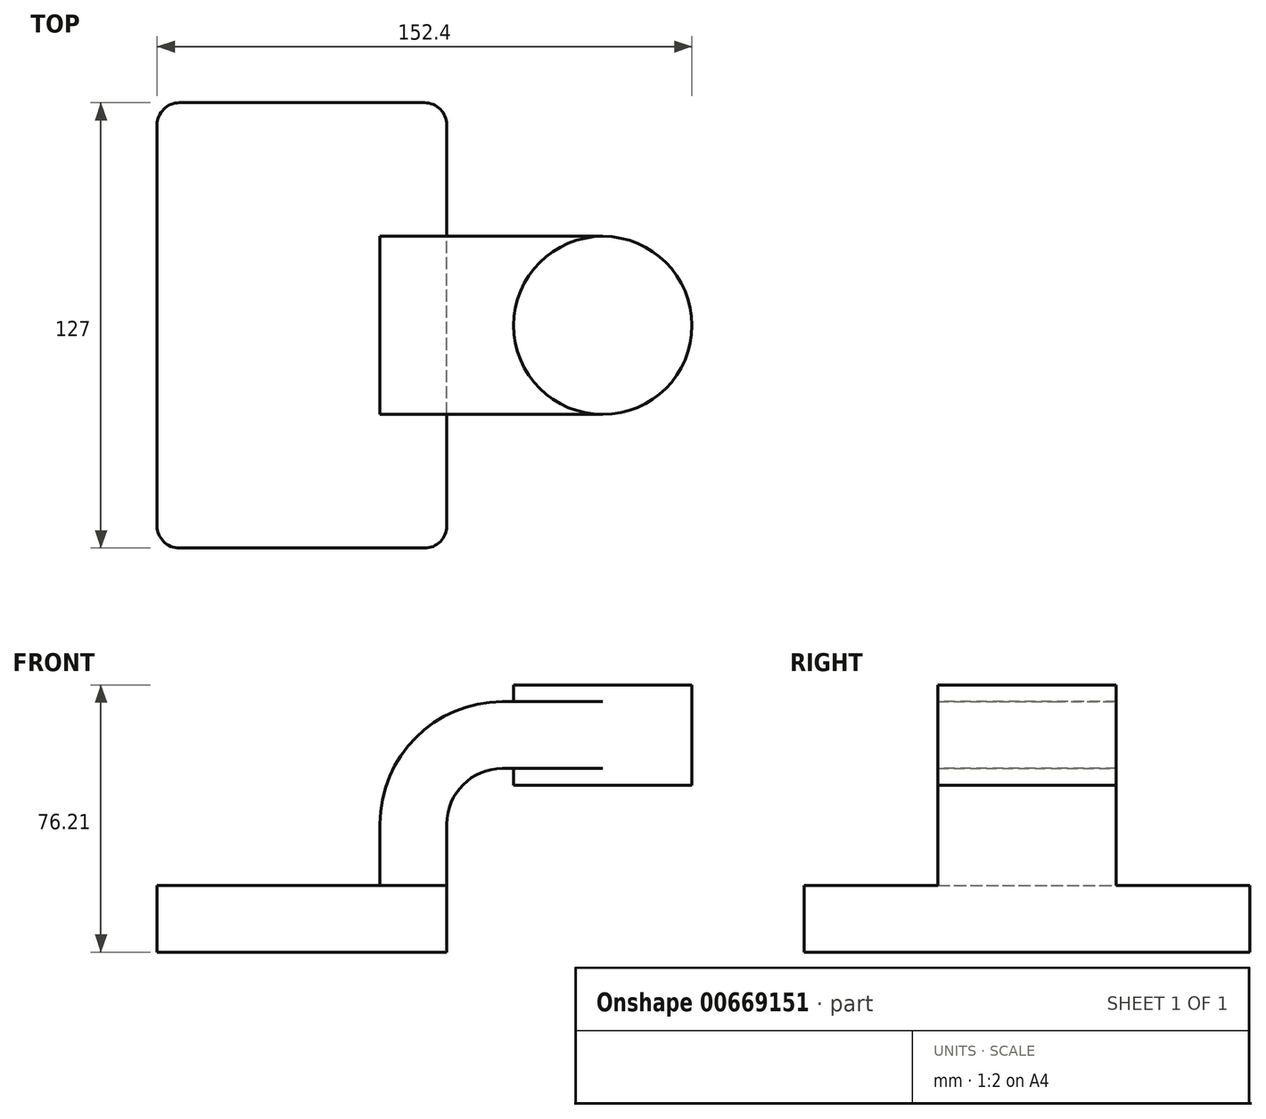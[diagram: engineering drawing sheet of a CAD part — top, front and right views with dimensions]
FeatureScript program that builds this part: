
annotation { "Feature Type Name" : "Feature", "Feature Type Description" : "" }
export const myFeature = defineFeature(function(context is Context, id is Id, definition is map)
    precondition{}
    {
        {
            var Q0;
            Q0=qCreatedBy(makeId("Front.planeOp"),FACE);
            var sketch = newSketch(context, id + "F0", { "sketchPlane" : qUnion([Q0])});
            skLineSegment(sketch, "E0.bottom", {"start": v(-41.28, 9.52) * mm, "end": v(41.28, 9.53) * mm});
            skLineSegment(sketch, "E0.top", {"start": v(-41.28, -9.53) * mm, "end": v(41.28, -9.53) * mm});
            skLineSegment(sketch, "E0.left", {"start": v(-41.28, 9.52) * mm, "end": v(-41.28, -9.53) * mm});
            skLineSegment(sketch, "E0.right", {"start": v(41.28, 9.53) * mm, "end": v(41.28, -9.52) * mm});
            skPoint(sketch, "E0.middle", {"position": v(0, 0) * mm});
            skLineSegment(sketch, "E1.bottom", {"start": v(60.32, 66.67) * mm, "end": v(111.12, 66.67) * mm});
            skLineSegment(sketch, "E1.top", {"start": v(60.32, 38.1) * mm, "end": v(111.12, 38.1) * mm});
            skLineSegment(sketch, "E1.left", {"start": v(60.32, 66.67) * mm, "end": v(60.32, 38.1) * mm});
            skLineSegment(sketch, "E1.right", {"start": v(111.12, 66.67) * mm, "end": v(111.12, 38.1) * mm});
            skPoint(sketch, "E1.middle", {"position": v(85.72, 52.39) * mm});
            skLineSegment(sketch, "E2", {"start": v(41.27, 9.53) * mm, "end": v(41.27, 26.99) * mm});
            skArc(sketch, "E3", {"start": v(41.27, 26.99) * mm, "mid": v(45.92, 38.21) * mm, "end": v(57.15, 42.86) * mm});
            skLineSegment(sketch, "E4", {"start": v(57.15, 42.86) * mm, "end": v(85.72, 42.86) * mm});
            skLineSegment(sketch, "E5.0", {"start": v(57.15, 61.91) * mm, "end": v(85.72, 61.91) * mm});
            skArc(sketch, "E5.1", {"start": v(22.23, 26.99) * mm, "mid": v(32.45, 51.68) * mm, "end": v(57.15, 61.91) * mm});
            skLineSegment(sketch, "E5.2", {"start": v(22.22, 9.53) * mm, "end": v(22.22, 26.99) * mm});
            skFitSpline(sketch, "E6", {"points": [v(-41.28, 9.52) * mm, v(57.15, 61.91) * mm], "startDerivative": vector(60.01, 126.68) * mm, "endDerivative": vector(125.56, 0.13) * mm});
            skLineSegment(sketch, "E7", {"start": v(85.72, 66.67) * mm, "end": v(85.72, 38.1) * mm});
            skSolve(sketch);
        }
        {
            var Q0;
            Q0=makeQuery(id+"F0.imprint","IMPRINT",FACE,{"disambiguationData":[TD([[makeQuery(id+"F0.imprint","IMPRINT",EDGE,{"derivedFrom":sQuery(id+"F0.wireOp",EDGE,"E0.top")}),1.0]])]});
            extrude(context, id + "F1", {"entities" : qUnion([Q0]), "endBound" : BoundingType.SYMMETRIC, "depth" : 127 * mm, "offsetDistance" : 25.4 * mm});
        }
        {
            var Q0;
            {var subQ1=sQuery(id+"F0.wireOp",EDGE,"E2");Q0=makeQuery(id+"F0.imprint","IMPRINT",FACE,{"disambiguationData":[TD([[makeQuery(id+"F0.imprint","IMPRINT",EDGE,{"derivedFrom":subQ1}),1.0]])]});}
            var Q1;
            {var subQ0=sQuery(id+"F0.wireOp",EDGE,"E5.0");var subQ1=sQuery(id+"F0.wireOp",EDGE,"E1.left");var subQ2=makeQuery(id+"F0.imprint","INTERSECT",VERTEX,{"derivedFrom":[subQ1,subQ0]});Q1=makeQuery(id+"F0.imprint","IMPRINT",FACE,{"disambiguationData":[TD([[makeQuery(id+"F0.imprint","IMPRINT",EDGE,{"disambiguationData":[TD([[subQ2,-1.0]])],"derivedFrom":subQ1}),1.0]])]});}
            extrude(context, id + "F2", {"entities" : qUnion([Q0, Q1]), "operationType" : NewBodyOperationType.ADD, "endBound" : BoundingType.SYMMETRIC, "depth" : 50.8 * mm, "offsetDistance" : 25.4 * mm});
        }
        {
            var Q0;
            {var subQ4=sQuery(id+"F0.wireOp",EDGE,"E5.1");Q0=makeQuery(id+"F0.imprint","IMPRINT",FACE,{"disambiguationData":[TD([[makeQuery(id+"F0.imprint","IMPRINT",EDGE,{"derivedFrom":subQ4}),1.0]])]});}
            extrude(context, id + "F3", {"entities" : qUnion([Q0]), "operationType" : NewBodyOperationType.ADD, "endBound" : BoundingType.SYMMETRIC, "depth" : 15.88 * mm, "offsetDistance" : 25.4 * mm});
        }
        {
            var Q0;
            {var subQ0=sQuery(id+"F0.wireOp",EDGE,"E1.right");Q0=makeQuery(id+"F0.imprint","IMPRINT",FACE,{"disambiguationData":[TD([[makeQuery(id+"F0.imprint","IMPRINT",EDGE,{"derivedFrom":subQ0}),-1.0]])]});}
            var Q1;
            Q1=sQuery(id+"F0.wireOp",EDGE,"E7");
            revolve(context, id + "F4", {"operationType" : NewBodyOperationType.ADD, "entities" : qUnion([Q0]), "axis" : qUnion([Q1]), "revolveType" : RevolveType.FULL});
        }
        {
            var Q0;
            Q0=makeQuery(id+"F1.opExtrude","CAP_EDGE",EDGE,{"disambiguationData":[OSD([sQuery(id+"F0.wireOp",EDGE,"E0.right")])],"isStart":false});
            var Q1;
            Q1=makeQuery(id+"F1.opExtrude","CAP_EDGE",EDGE,{"disambiguationData":[OSD([sQuery(id+"F0.wireOp",EDGE,"E0.left")])],"isStart":false});
            var Q2;
            Q2=makeQuery(id+"F1.opExtrude","CAP_EDGE",EDGE,{"disambiguationData":[OSD([sQuery(id+"F0.wireOp",EDGE,"E0.right")])],"isStart":true});
            var Q3;
            Q3=makeQuery(id+"F1.opExtrude","CAP_EDGE",EDGE,{"disambiguationData":[OSD([sQuery(id+"F0.wireOp",EDGE,"E0.left")])],"isStart":true});
            fillet(context, id + "F5", {"entities" : qUnion([Q0, Q1, Q2, Q3]), "radius" : 6.35 * mm, "tangentPropagation" : true, "allowEdgeOverflow" : false});
        }
    });
